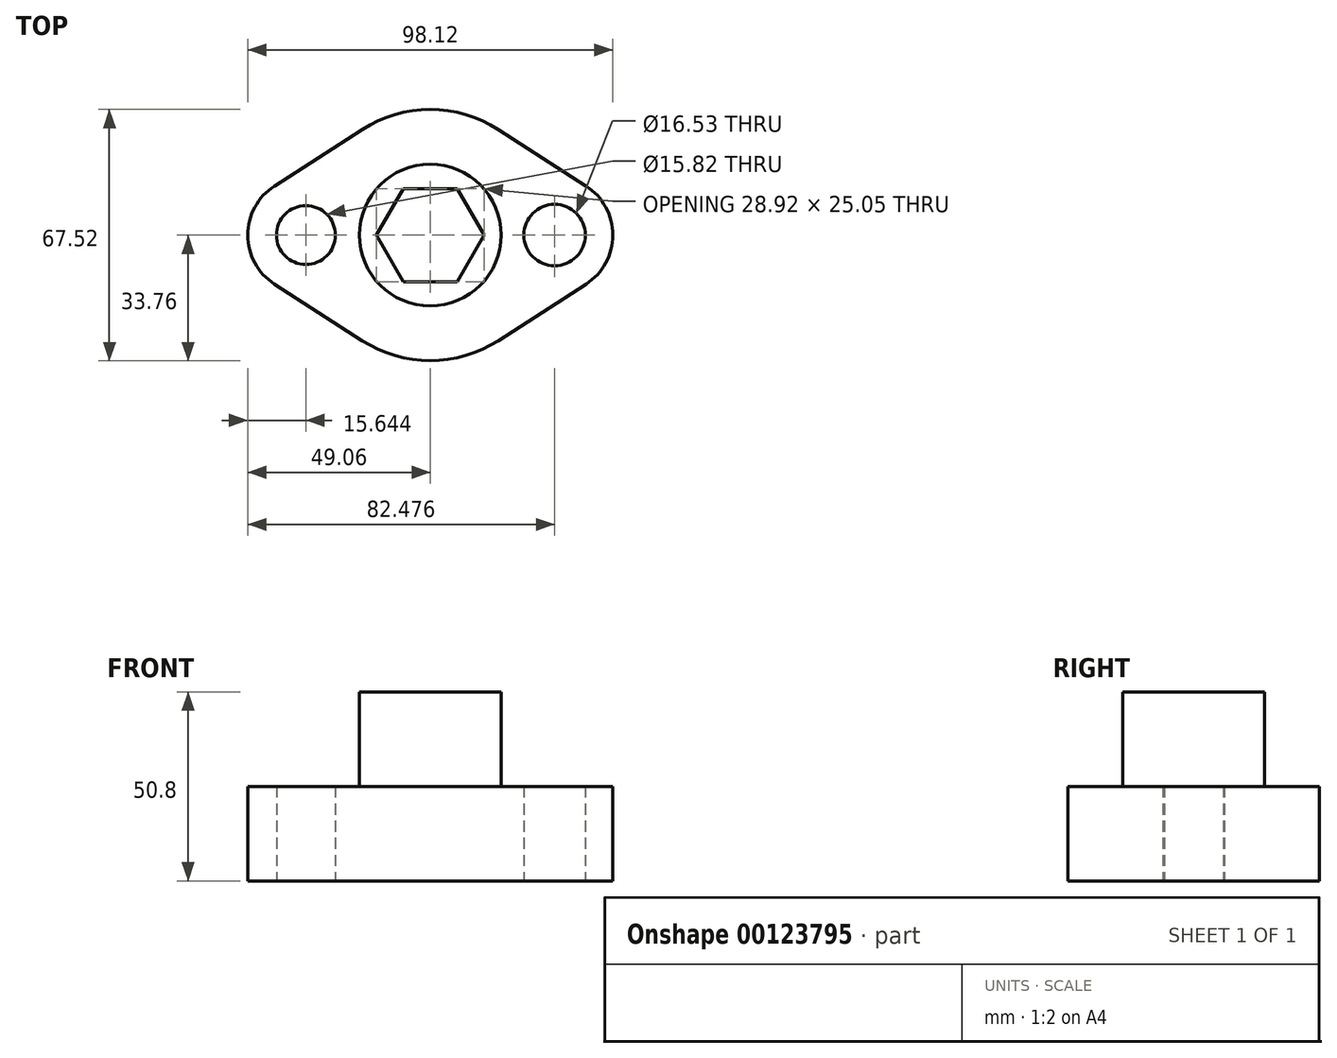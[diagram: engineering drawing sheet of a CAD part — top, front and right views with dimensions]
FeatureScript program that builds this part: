
annotation { "Feature Type Name" : "Feature", "Feature Type Description" : "" }
export const myFeature = defineFeature(function(context is Context, id is Id, definition is map)
    precondition{}
    {
        {
            var Q0;
            Q0=qCreatedBy(makeId("Top.planeOp"),FACE);
            var sketch = newSketch(context, id + "F0", { "sketchPlane" : qUnion([Q0])});
            skCircle(sketch, "E0", {"center": v(0, 0) * mm, "radius": 19.05 * mm});
            skCircle(sketch, "E1", {"center": v(33.42, 0) * mm, "radius": 8.27 * mm});
            skCircle(sketch, "E2", {"center": v(-33.42, 0) * mm, "radius": 7.91 * mm});
            skArc(sketch, "E3", {"start": v(18.3, 28.37) * mm, "mid": v(0, 33.76) * mm, "end": v(-18.3, 28.37) * mm});
            skArc(sketch, "E4", {"start": v(18.3, -28.37) * mm, "mid": v(0, -33.76) * mm, "end": v(-18.3, -28.37) * mm});
            skArc(sketch, "E5", {"start": v(41.9, 13.15) * mm, "mid": v(49.06, 0) * mm, "end": v(41.9, -13.15) * mm});
            skArc(sketch, "E6", {"start": v(-41.9, 13.15) * mm, "mid": v(-49.06, 0) * mm, "end": v(-41.9, -13.15) * mm});
            skLineSegment(sketch, "E7", {"start": v(-41.9, 13.15) * mm, "end": v(-18.3, 28.37) * mm});
            skLineSegment(sketch, "E8", {"start": v(18.3, 28.37) * mm, "end": v(41.9, 13.15) * mm});
            skLineSegment(sketch, "E9", {"start": v(41.9, -13.15) * mm, "end": v(18.3, -28.37) * mm});
            skLineSegment(sketch, "E10", {"start": v(-18.3, -28.37) * mm, "end": v(-41.9, -13.15) * mm});
            skCircle(sketch, "E11.cCircle", {"center": v(0, 0) * mm, "radius": 12.52 * mm, "construction": true});
            skLineSegment(sketch, "E11.0", {"start": v(-7.23, 12.52) * mm, "end": v(7.23, 12.52) * mm});
            skLineSegment(sketch, "E11.1", {"start": v(7.23, 12.52) * mm, "end": v(14.46, 0) * mm});
            skLineSegment(sketch, "E11.2", {"start": v(14.46, 0) * mm, "end": v(7.23, -12.52) * mm});
            skLineSegment(sketch, "E11.3", {"start": v(7.23, -12.52) * mm, "end": v(-7.23, -12.52) * mm});
            skLineSegment(sketch, "E11.4", {"start": v(-7.23, -12.52) * mm, "end": v(-14.46, 0) * mm});
            skLineSegment(sketch, "E11.5", {"start": v(-14.46, 0) * mm, "end": v(-7.23, 12.52) * mm});
            skPoint(sketch, "E11.0.midPoint", {"position": v(0, 12.52) * mm});
            skSolve(sketch);
        }
        {
            var Q0;
            Q0=makeQuery(id+"F0.imprint","IMPRINT",FACE,{"disambiguationData":[TD([[makeQuery(id+"F0.imprint","IMPRINT",EDGE,{"derivedFrom":sQuery(id+"F0.wireOp",EDGE,"E0")}),1.0]])]});
            extrude(context, id + "F1", {"entities" : qUnion([Q0]), "depth" : 50.8 * mm});
        }
        {
            var Q0;
            Q0=makeQuery(id+"F0.imprint","IMPRINT",FACE,{"disambiguationData":[TD([[makeQuery(id+"F0.imprint","IMPRINT",EDGE,{"derivedFrom":sQuery(id+"F0.wireOp",EDGE,"E0")}),-1.0]])]});
            extrude(context, id + "F2", {"entities" : qUnion([Q0]), "operationType" : NewBodyOperationType.ADD, "depth" : 25.4 * mm});
        }
    });
